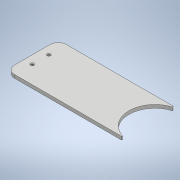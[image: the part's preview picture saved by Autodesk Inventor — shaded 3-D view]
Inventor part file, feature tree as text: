
AUTODESK INVENTOR PART (.ipt)
format: ipt  version: 2020 (Build 240168000, 168)  size: 127,488 bytes
history: native  units: mm
features: fillet x2, extrude x1, hole x1, sketch x1
ambient origin geometry x8: Origin, YZ Plane, XZ Plane, XY Plane, X Axis, Y Axis, Z Axis, Center Point
bodies: Body1 (feature_tree)
feature tree (5):
  extrude  "Выдавливание3"  Depth=11.0mm
  fillet  "Сопряжение3"  Radius=1.4mm
  fillet  "Сопряжение4"  Radius=41.0mm
  hole  "Отверстие1"  [1 undecoded]
  sketch  "Эскиз6"
note: 1 required parameter value undecoded (feature->parameter linkage not recoverable at this tier; creation-order binding heuristic only, values carry confidence <= 0.55)
